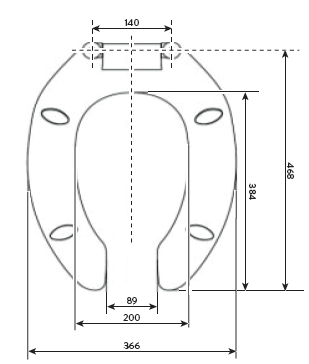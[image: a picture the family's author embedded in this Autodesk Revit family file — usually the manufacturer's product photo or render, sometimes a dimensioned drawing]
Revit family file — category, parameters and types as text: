
# Revit family: Ducha Antivandálica con Regadera Empotrada
name_source: partatom
category: Plumbing Fixtures
units: mm (PartAtom-declared; Revit-internal decimal feet)

## family parameters
Always vertical = Yes
Cut with Voids When Loaded = No
Host = Wall
OmniClass Number = 23.31.11.00
Part Type = Normal
Room Calculation Point = No
Round Connector Dimension = Use Diameter
Shared = No

## types (1)
- Type 1
    Alto = 74 mm  [stored 0.242782 ft]
    Capacidad de flujo = 9,68 L/min - 0,49 L/Descarga.
    Creado por = BIMBAU
    Default Elevation = 0 mm  [stored 0 ft]
    Description = Este producto es el aliado perfecto para las necesidades de las instituciones de alto tráfico. Disfruta de su óptimo funcionamiento y durabilidad debido a sus características antivandálicas.
    Diámetro = 74 mm  [stored 0.242782 ft]
    Entrada minimo = 1/2 NPT
    Fecha de creación = 12/03/2021
    Garantía = 3 años
    Manufacturer = Corona
    Material = Corona_Cromo
    Material 2 = Corona_Cobre
    Model = Cuerpo Ducha Antivandalica
    Peso  Bruto = 690g 1,52lb.
    Peso neto = 617g 1,36lb.
    Presión máxima recomendada = 80 Psi.
    Presión mínima recomendada = 20 Psi.
    Profundidad = 90 mm
    Referencia = 704310001
    URL = https://corona.co
    Vida útil = 150 Mil Ciclos.

note: [stored X ft] marks values corroborated as IEEE doubles in the binary element streams (Revit-internal decimal feet)

## geometry (parser evidence)
native form markers: Sweep x7
no freeform markers — native parametric forms only
